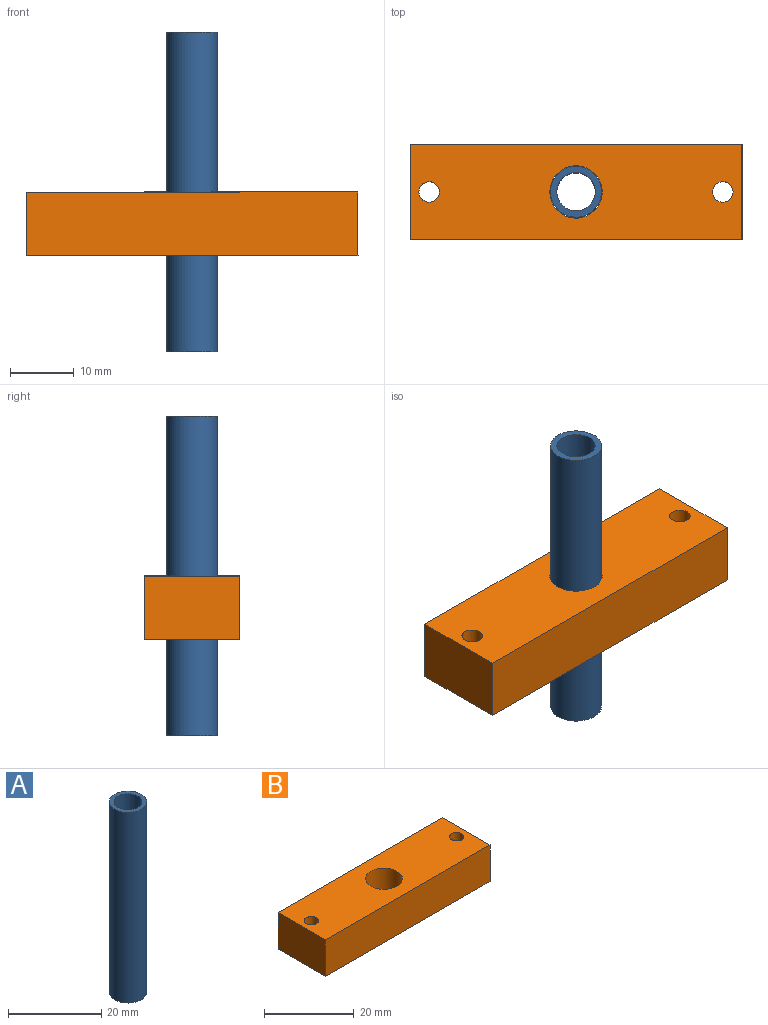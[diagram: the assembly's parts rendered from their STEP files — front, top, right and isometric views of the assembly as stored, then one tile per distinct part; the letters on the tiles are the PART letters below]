
ASSEMBLY  parts=2 mates=1
PART A: 4 faces, bbox 8x8x50 mm
  f0: cylinder r=3mm len=50mm, axis (0,0,-1), area 942.5mm2, adj f2,f3
  f1: cylinder r=4mm len=50mm, axis (0,0,-1), area 1256.6mm2, adj f2,f3
  f2: plane 8x8mm, normal (0,0,1), area 22mm2, adj f0,f1
  f3: plane 8x8mm, normal (0,0,-1), area 22mm2, adj f0,f1
PART B: 9 faces, bbox 52x15x10 mm
  f0: plane 15x10mm, normal (1,0,0), area 150mm2, adj f1,f4,f6,f7
  f1: plane 52x10mm, normal (0,1,0), area 520mm2, adj f0,f2,f6,f7
  f2: plane 15x10mm, normal (-1,0,0), area 150mm2, adj f1,f4,f6,f7
  f3: cylinder r=1.6mm len=10mm, axis (0,0,-1), area 100.5mm2, adj f6,f7
  f4: plane 52x10mm, normal (0,-1,0), area 520mm2, adj f0,f2,f6,f7
  f5: cylinder r=1.6mm len=10mm, axis (0,0,-1), area 100.5mm2, adj f6,f7
  f6: plane 52x15mm, normal (0,0,1), area 711.1mm2, adj f0,f1,f2,f3,f4,f5,f8
  f7: plane 52x15mm, normal (0,0,-1), area 711.1mm2, adj f0,f1,f2,f3,f4,f5,f8
  f8: cylinder r=4.1mm len=10mm, axis (0,0,1), area 257.6mm2, adj f6,f7
PLACE A t=(8.86,-14.73,-48.39)mm
PLACE B t=(8.86,-14.73,-33.39)mm
MATE fastened A.f0 <-> B.f8  axis (0,0,1) through (8.86,-14.73,1.61)mm
